SOLIDWORKS PART (.sldprt)
format: sldprt  version: not decoded by parser v0  size: 248,832 bytes
history: native  units: mm
features: sketch x7, plane x3, extrude x3, cut_extrude x2, material x1, revolve x1, fillet x1, cut_revolve x1 (+8 scaffold rows collapsed)
feature tree (27):
  scaffold x8  (default folders/planes/origin — collapsed)
  material  "Matériau <non spécifié>"
  plane  "Face"
  plane  "Dessus"
  plane  "Droite"
  sketch  "Esquisse1"  dims[D1=8.0mm D2=12.5mm]
  revolve  "Révolution1"  Angle=360deg
  sketch  "Esquisse2"  dims[D1=9.5mm D2=7.6mm]
  extrude  "Extrusion1"  Depth=22.5mm
  sketch  "Esquisse3"  dims[D1=14.0mm D2=0.7mm]
  extrude  "Extrusion2"  Depth=1mm
  fillet  "Congé1"  Radius=1mm
  sketch  "Esquisse4"  dims[c1.D1=0.05mm c1.D2=0.05mm c1.D3=0.05mm c1.D4=0.2mm c1.D5=0.2mm c1.D6=~2.432376mm c2.D6=~179.774169deg c3.D6=1.0mm c3.D7=1.0mm c3.D8=1.0mm c3.D9=6.5mm c3.D10=9.0mm c3.D11=0.3mm c3.D12=~1.25071mm c4.D12=45.0deg c4.D13=~6.372822mm c5.D13=45.0deg c5.D14=0.7mm c5.D15=8.75mm c5.D16=1.0mm c5.D17=4.5mm c5.D11=1.0mm c6.D16=1.0mm c6.D9=1.0mm c7.D16=0.3mm c7.D18=1.0mm]
  extrude  "Extrusion4"  Depth=3.8mm
  sketch  "Esquisse5"
  cut_extrude  "Enlèv. mat.-Extru.1"  Depth=0.25mm
  sketch  "Esquisse6"  dims[c1.D1=8.0mm c1.D2=~6.468989mm c2.D2=~175.399904deg c3.D2=7.1mm c3.D3=~6.468989mm c4.D3=5.0deg]
  cut_revolve  "Enlèvement de matière-Révolution1"  Angle=360deg
  sketch  "Esquisse7"  dims[D1=5.0mm]
  cut_extrude  "Enlèv. mat.-Extru.2"  Depth=13mm
decode coverage: 14 of 15 modeling features carry decoded parameters
note: ~ marks probable driven/reference dimensions
note: suppression state not decoded; provenance and decode notes live in map.json
